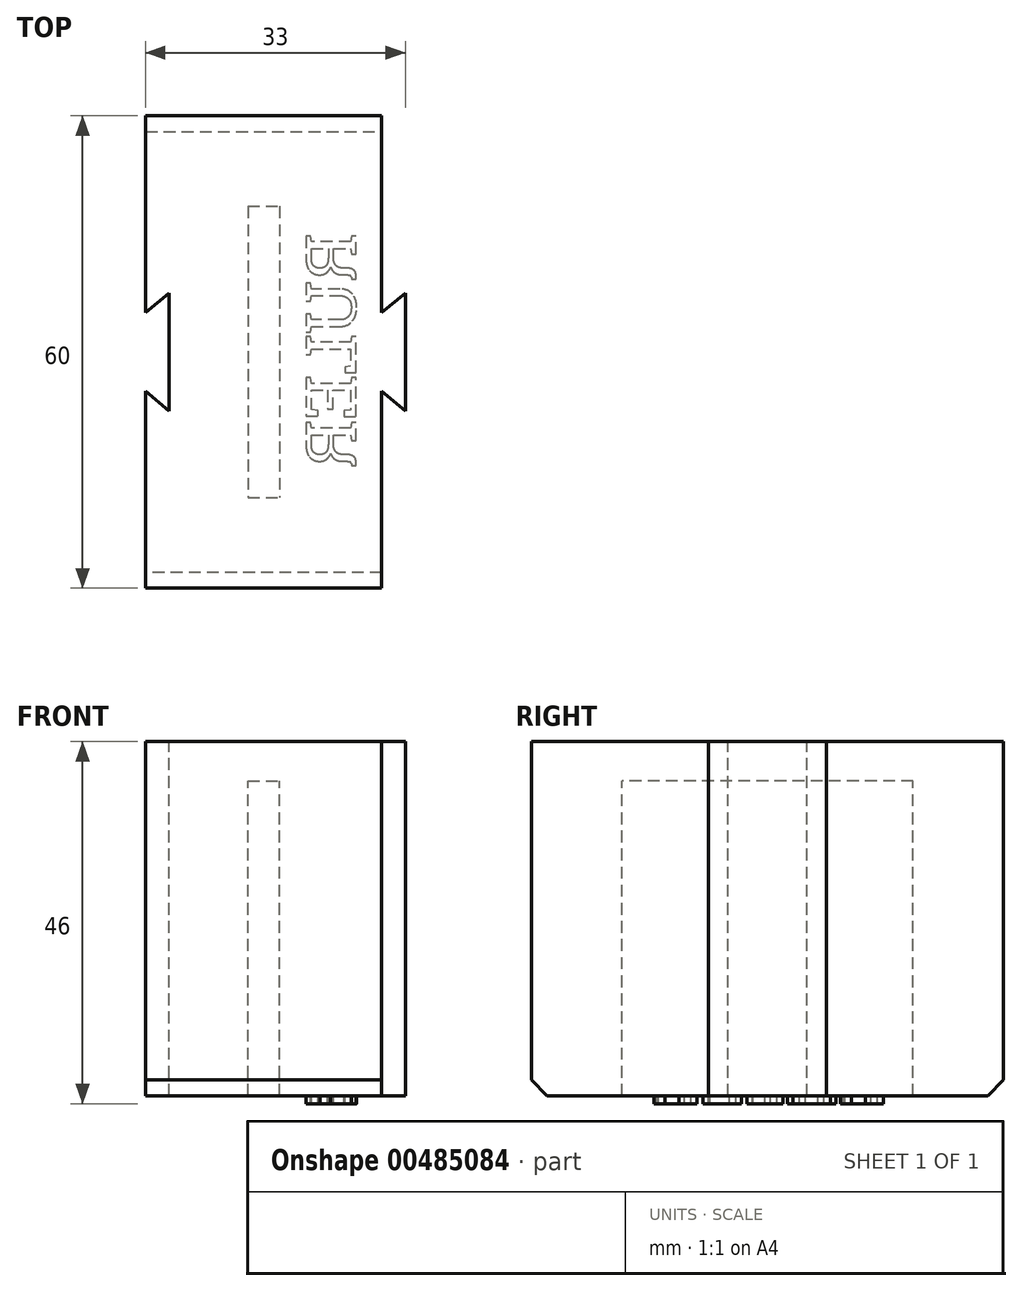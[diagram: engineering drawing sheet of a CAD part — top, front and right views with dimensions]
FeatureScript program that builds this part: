
annotation { "Feature Type Name" : "Feature", "Feature Type Description" : "" }
export const myFeature = defineFeature(function(context is Context, id is Id, definition is map)
    precondition{}
    {
        {
            var Q0;
            Q0=qCreatedBy(makeId("Top.planeOp"),FACE);
            var sketch = newSketch(context, id + "F0", { "sketchPlane" : qUnion([Q0])});
            skPoint(sketch, "E0.middle", {"position": v(0, 0) * mm});
            skLineSegment(sketch, "E1.bottom", {"start": v(15, 30) * mm, "end": v(-15, 30) * mm});
            skLineSegment(sketch, "E1.top", {"start": v(15, -30) * mm, "end": v(-15, -30) * mm});
            skLineSegment(sketch, "E2.left", {"start": v(-12, 7.5) * mm, "end": v(-12, -7.5) * mm});
            skLineSegment(sketch, "E3.left", {"start": v(18, 7.5) * mm, "end": v(18, -7.5) * mm});
            skLineSegment(sketch, "E4", {"start": v(-12, 7.5) * mm, "end": v(-15, 5) * mm});
            skLineSegment(sketch, "E5", {"start": v(15, 30) * mm, "end": v(15, 5) * mm});
            skLineSegment(sketch, "E6", {"start": v(15, -5) * mm, "end": v(15, -30) * mm});
            skLineSegment(sketch, "E7", {"start": v(-15, -30) * mm, "end": v(-15, -5) * mm});
            skLineSegment(sketch, "E8", {"start": v(-12, -7.5) * mm, "end": v(-12, 7.5) * mm});
            skLineSegment(sketch, "E9", {"start": v(-15, -5) * mm, "end": v(-12, -7.5) * mm});
            skLineSegment(sketch, "E10", {"start": v(-15, 5) * mm, "end": v(-15, 30) * mm});
            skLineSegment(sketch, "E11", {"start": v(15, 5) * mm, "end": v(18, 7.5) * mm});
            skLineSegment(sketch, "E12", {"start": v(15, -5) * mm, "end": v(18, -7.5) * mm});
            skLineSegment(sketch, "E13.bottom", {"start": v(-2, 18.5) * mm, "end": v(2, 18.5) * mm});
            skLineSegment(sketch, "E13.top", {"start": v(-2, -18.5) * mm, "end": v(2, -18.5) * mm});
            skLineSegment(sketch, "E13.left", {"start": v(-2, 18.5) * mm, "end": v(-2, -18.5) * mm});
            skLineSegment(sketch, "E13.right", {"start": v(2, 18.5) * mm, "end": v(2, -18.5) * mm});
            skSolve(sketch);
        }
        {
            var Q0;
            Q0=makeQuery(id+"F0.imprint","IMPRINT",FACE,{"disambiguationData":[TD([[makeQuery(id+"F0.imprint","IMPRINT",EDGE,{"derivedFrom":sQuery(id+"F0.wireOp",EDGE,"E1.bottom")}),1.0]])]});
            extrude(context, id + "F1", {"entities" : qUnion([Q0]), "oppositeDirection" : true, "depth" : 40 * mm});
        }
        {
            var Q0;
            Q0=makeQuery(id+"F0.imprint","IMPRINT",FACE,{"disambiguationData":[TD([[makeQuery(id+"F0.imprint","IMPRINT",EDGE,{"derivedFrom":sQuery(id+"F0.wireOp",EDGE,"E13.bottom")}),-1.0]])]});
            var Q1;
            Q1=makeQuery(id+"F0.imprint","IMPRINT",FACE,{"disambiguationData":[TD([[makeQuery(id+"F0.imprint","IMPRINT",EDGE,{"derivedFrom":sQuery(id+"F0.wireOp",EDGE,"E1.bottom")}),1.0]])]});
            extrude(context, id + "F2", {"entities" : qUnion([Q0, Q1]), "operationType" : NewBodyOperationType.ADD, "depth" : 5 * mm});
        }
        {
            var Q0;
            Q0=makeQuery(id+"F1.opExtrude","CAP_FACE",FACE,{"disambiguationData":[OSD([sQuery(id+"F0.wireOp",EDGE,"E1.bottom"),sQuery(id+"F0.wireOp",EDGE,"E1.top"),sQuery(id+"F0.wireOp",EDGE,"E4"),sQuery(id+"F0.wireOp",EDGE,"E5"),sQuery(id+"F0.wireOp",EDGE,"E3.left"),sQuery(id+"F0.wireOp",EDGE,"E6"),sQuery(id+"F0.wireOp",EDGE,"E7"),sQuery(id+"F0.wireOp",EDGE,"E8"),sQuery(id+"F0.wireOp",EDGE,"E9"),sQuery(id+"F0.wireOp",EDGE,"E10"),sQuery(id+"F0.wireOp",EDGE,"E11"),sQuery(id+"F0.wireOp",EDGE,"E12"),sQuery(id+"F0.wireOp",EDGE,"E13.bottom"),sQuery(id+"F0.wireOp",EDGE,"E13.top"),sQuery(id+"F0.wireOp",EDGE,"E13.left"),sQuery(id+"F0.wireOp",EDGE,"E13.right")])],"isStart":false});
            var sketch = newSketch(context, id + "F3", { "sketchPlane" : qUnion([Q0])});
            skText(sketch, "E14", { "text": "RULER", "fontName": "RobotoSlab-Regular.ttf"});
            const initialGuessF3  = {"E14": [0.01173, -0.01502, 0, 1, 0.00643]};
            skSetInitialGuess(sketch, initialGuessF3);
            skSolve(sketch);
        }
        {
            var Q0;
            Q0 = qSketchRegion(id + "F3", true);
            extrude(context, id + "F4", {"entities" : qUnion([Q0]), "operationType" : NewBodyOperationType.ADD, "depth" : 1 * mm});
        }
        {
            var Q0;
            Q0=makeQuery(id+"F1.opExtrude","CAP_EDGE",EDGE,{"disambiguationData":[OSD([sQuery(id+"F0.wireOp",EDGE,"E1.bottom")])],"isStart":false});
            var Q1;
            Q1=makeQuery(id+"F1.opExtrude","CAP_EDGE",EDGE,{"disambiguationData":[OSD([sQuery(id+"F0.wireOp",EDGE,"E1.top")])],"isStart":false});
            chamfer(context, id + "F5", {"entities" : qUnion([Q0, Q1]), "width" : 2 * mm, "tangentPropagation" : true});
        }
    });
